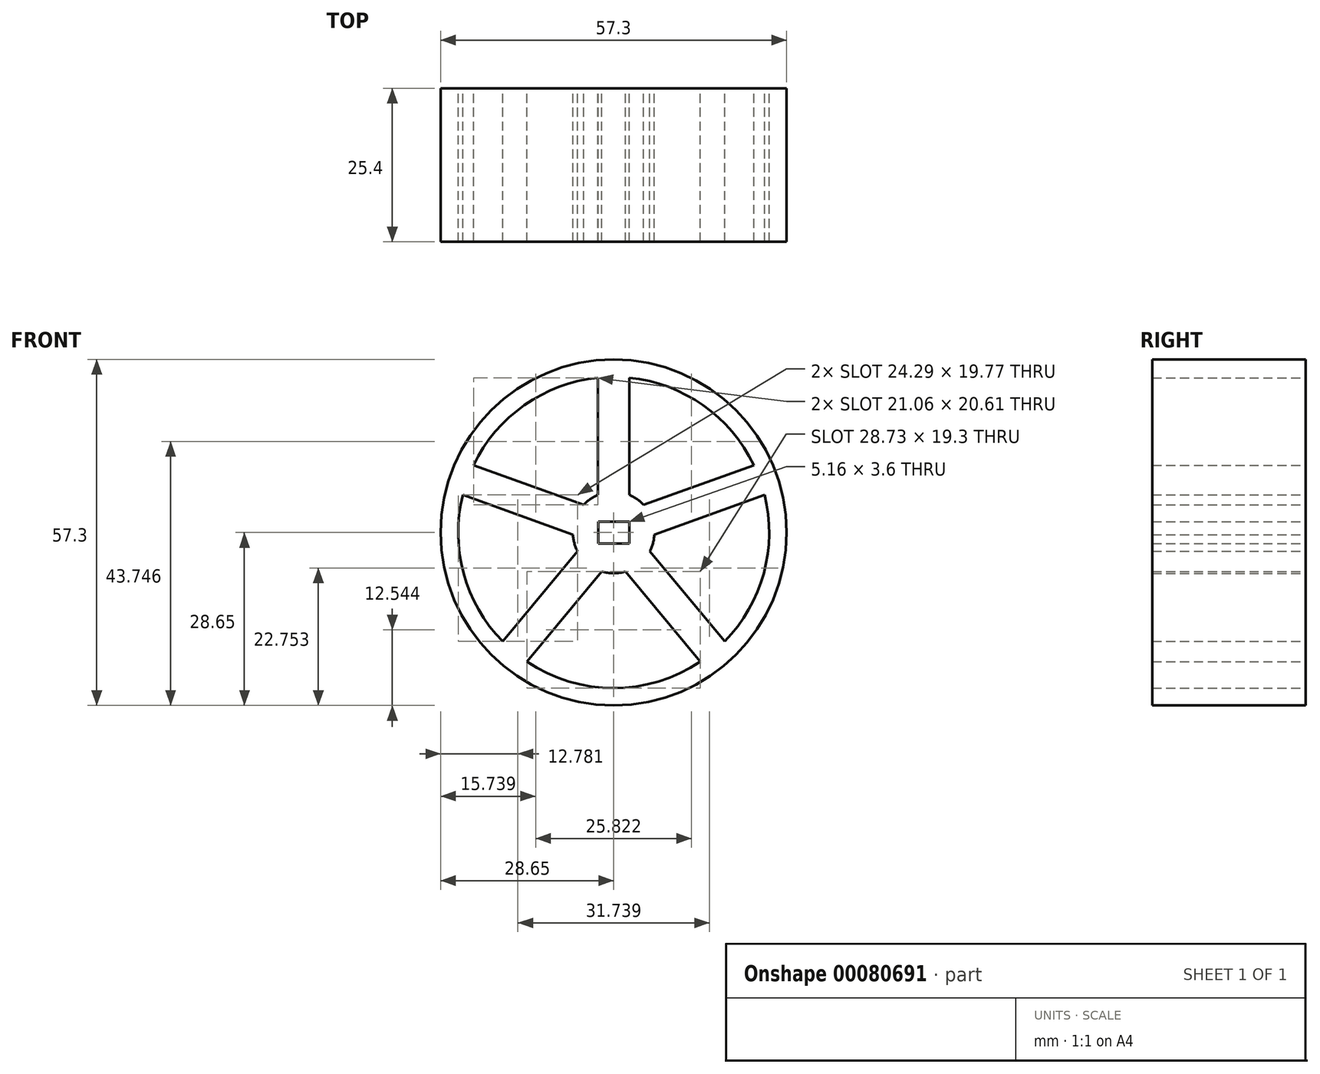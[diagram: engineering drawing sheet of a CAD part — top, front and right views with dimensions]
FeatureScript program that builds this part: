
annotation { "Feature Type Name" : "Feature", "Feature Type Description" : "" }
export const myFeature = defineFeature(function(context is Context, id is Id, definition is map)
    precondition{}
    {
        {
            var Q0;
            Q0=qCreatedBy(makeId("Front.planeOp"),FACE);
            var sketch = newSketch(context, id + "F0", { "sketchPlane" : qUnion([Q0])});
            skCircle(sketch, "E0", {"center": v(0, 0) * mm, "radius": 25.76 * mm});
            skCircle(sketch, "E1", {"center": v(0, 0) * mm, "radius": 6.75 * mm});
            skLineSegment(sketch, "E2", {"start": v(-2.6, 25.62) * mm, "end": v(-2.6, 6.23) * mm});
            skLineSegment(sketch, "E3.MirrorCS", {"start": v(2.6, 25.62) * mm, "end": v(2.6, 6.23) * mm});
            skLineSegment(sketch, "E4.1.0", {"start": v(23.21, 11.16) * mm, "end": v(4.97, 4.57) * mm});
            skLineSegment(sketch, "E4.1.1", {"start": v(24.99, 6.25) * mm, "end": v(6.74, -0.34) * mm});
            skLineSegment(sketch, "E4.2.0", {"start": v(18.38, -18.04) * mm, "end": v(5.98, -3.12) * mm});
            skLineSegment(sketch, "E4.2.1", {"start": v(14.37, -21.38) * mm, "end": v(1.97, -6.46) * mm});
            skLineSegment(sketch, "E4.anchor1", {"start": v(0, 0) * mm, "end": v(-2.6, 6.23) * mm, "construction": true});
            skLineSegment(sketch, "E4.anchor2", {"start": v(0, 0) * mm, "end": v(5.98, -3.12) * mm, "construction": true});
            skLineSegment(sketch, "E5.MirrorCS", {"start": v(-23.21, 11.16) * mm, "end": v(-4.97, 4.57) * mm});
            skLineSegment(sketch, "E6.MirrorCS", {"start": v(-24.99, 6.25) * mm, "end": v(-6.74, -0.34) * mm});
            skLineSegment(sketch, "E7.MirrorCS", {"start": v(-18.38, -18.04) * mm, "end": v(-5.98, -3.12) * mm});
            skLineSegment(sketch, "E8.MirrorCS", {"start": v(-14.37, -21.38) * mm, "end": v(-1.97, -6.46) * mm});
            skCircle(sketch, "E9", {"center": v(0, 0) * mm, "radius": 28.65 * mm});
            skLineSegment(sketch, "E10.bottom", {"start": v(2.58, 1.8) * mm, "end": v(-2.58, 1.8) * mm});
            skLineSegment(sketch, "E10.top", {"start": v(2.58, -1.8) * mm, "end": v(-2.58, -1.8) * mm});
            skLineSegment(sketch, "E10.left", {"start": v(2.58, 1.8) * mm, "end": v(2.58, -1.8) * mm});
            skLineSegment(sketch, "E10.right", {"start": v(-2.58, 1.8) * mm, "end": v(-2.58, -1.8) * mm});
            skSolve(sketch);
        }
        {
            var Q0;
            Q0=makeQuery(id+"F0.imprint","IMPRINT",FACE,{"disambiguationData":[TD([[makeQuery(id+"F0.imprint","IMPRINT",EDGE,{"derivedFrom":sQuery(id+"F0.wireOp",EDGE,"E9")}),1.0]])]});
            var Q1;
            {var subQ0=sQuery(id+"F0.wireOp",EDGE,"E2");Q1=makeQuery(id+"F0.imprint","IMPRINT",FACE,{"disambiguationData":[TD([[makeQuery(id+"F0.imprint","IMPRINT",EDGE,{"derivedFrom":subQ0}),1.0]])]});}
            var Q2;
            {var subQ0=sQuery(id+"F0.wireOp",EDGE,"E4.1.0");Q2=makeQuery(id+"F0.imprint","IMPRINT",FACE,{"disambiguationData":[TD([[makeQuery(id+"F0.imprint","IMPRINT",EDGE,{"derivedFrom":subQ0}),1.0]])]});}
            var Q3;
            Q3=makeQuery(id+"F0.imprint","IMPRINT",FACE,{"disambiguationData":[TD([[makeQuery(id+"F0.imprint","IMPRINT",EDGE,{"derivedFrom":sQuery(id+"F0.wireOp",EDGE,"E10.bottom")}),-1.0]])]});
            var Q4;
            {var subQ0=sQuery(id+"F0.wireOp",EDGE,"E4.2.0");Q4=makeQuery(id+"F0.imprint","IMPRINT",FACE,{"disambiguationData":[TD([[makeQuery(id+"F0.imprint","IMPRINT",EDGE,{"derivedFrom":subQ0}),1.0]])]});}
            var Q5;
            {var subQ0=sQuery(id+"F0.wireOp",EDGE,"E7.MirrorCS");Q5=makeQuery(id+"F0.imprint","IMPRINT",FACE,{"disambiguationData":[TD([[makeQuery(id+"F0.imprint","IMPRINT",EDGE,{"derivedFrom":subQ0}),-1.0]])]});}
            var Q6;
            {var subQ0=sQuery(id+"F0.wireOp",EDGE,"E5.MirrorCS");Q6=makeQuery(id+"F0.imprint","IMPRINT",FACE,{"disambiguationData":[TD([[makeQuery(id+"F0.imprint","IMPRINT",EDGE,{"derivedFrom":subQ0}),-1.0]])]});}
            extrude(context, id + "F1", {"entities" : qUnion([Q0, Q1, Q2, Q3, Q4, Q5, Q6]), "depth" : 25.4 * mm});
        }
    });
